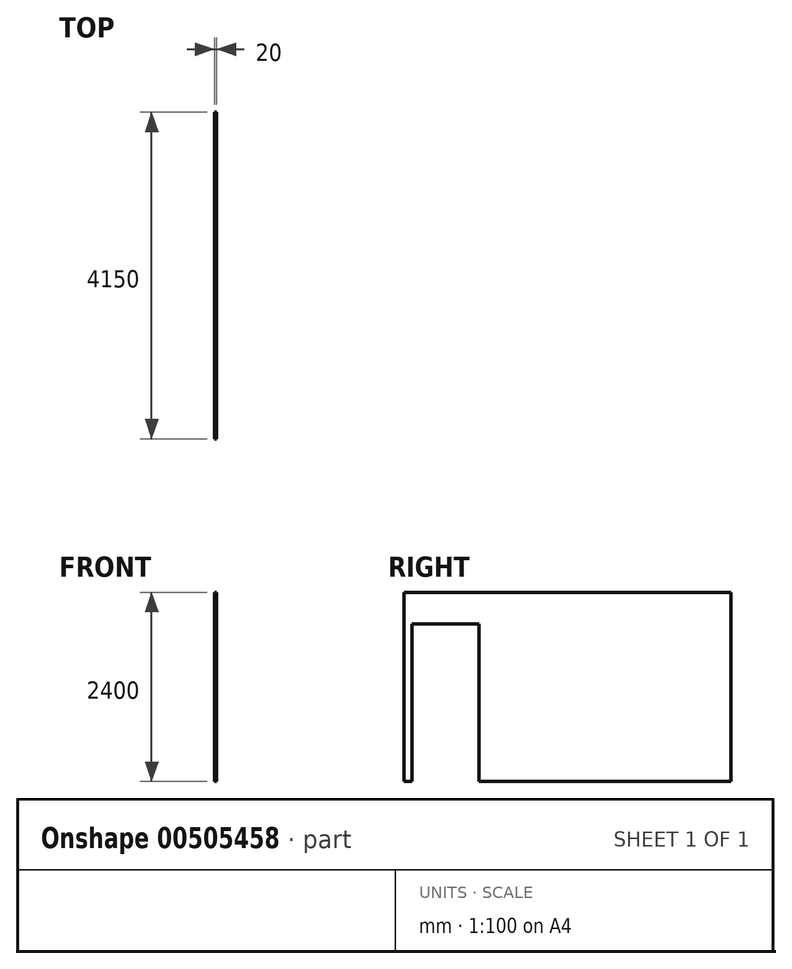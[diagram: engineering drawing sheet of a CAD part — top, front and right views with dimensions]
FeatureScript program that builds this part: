
annotation { "Feature Type Name" : "Feature", "Feature Type Description" : "" }
export const myFeature = defineFeature(function(context is Context, id is Id, definition is map)
    precondition{}
    {
        {
            var Q0;
            Q0=qCreatedBy(makeId("Top.planeOp"),FACE);
            var sketch = newSketch(context, id + "F0", { "sketchPlane" : qUnion([Q0])});
            skLineSegment(sketch, "E0.bottom", {"start": v(-10, 2075) * mm, "end": v(10, 2075) * mm});
            skLineSegment(sketch, "E0.top", {"start": v(-10, -2075) * mm, "end": v(10, -2075) * mm});
            skLineSegment(sketch, "E0.left", {"start": v(-10, 2075) * mm, "end": v(-10, -2075) * mm});
            skLineSegment(sketch, "E0.right", {"start": v(10, 2075) * mm, "end": v(10, -2075) * mm});
            skPoint(sketch, "E0.middle", {"position": v(0, 0) * mm});
            skSolve(sketch);
        }
        {
            var Q0;
            Q0 = qSketchRegion(id + "F0", true);
            extrude(context, id + "F1", {"entities" : qUnion([Q0]), "depth" : 2400 * mm});
        }
        {
            var Q0;
            Q0=makeQuery(id+"F1.opExtrude","SWEPT_FACE",FACE,{"disambiguationData":[OSD([sQuery(id+"F0.wireOp",EDGE,"E0.right")])]});
            var sketch = newSketch(context, id + "F2", { "sketchPlane" : qUnion([Q0])});
            skLineSegment(sketch, "E1.bottom", {"start": v(-1975, 0) * mm, "end": v(-1125, 0) * mm});
            skLineSegment(sketch, "E1.top", {"start": v(-1975, 2000) * mm, "end": v(-1125, 2000) * mm});
            skLineSegment(sketch, "E1.left", {"start": v(-1975, 0) * mm, "end": v(-1975, 2000) * mm});
            skLineSegment(sketch, "E1.right", {"start": v(-1125, 0) * mm, "end": v(-1125, 2000) * mm});
            skSolve(sketch);
        }
        {
            var Q0;
            Q0 = qSketchRegion(id + "F2", true);
            extrude(context, id + "F3", {"entities" : qUnion([Q0]), "operationType" : NewBodyOperationType.REMOVE, "endBound" : BoundingType.UP_TO_NEXT, "oppositeDirection" : true, "depth" : 25 * mm});
        }
    });
